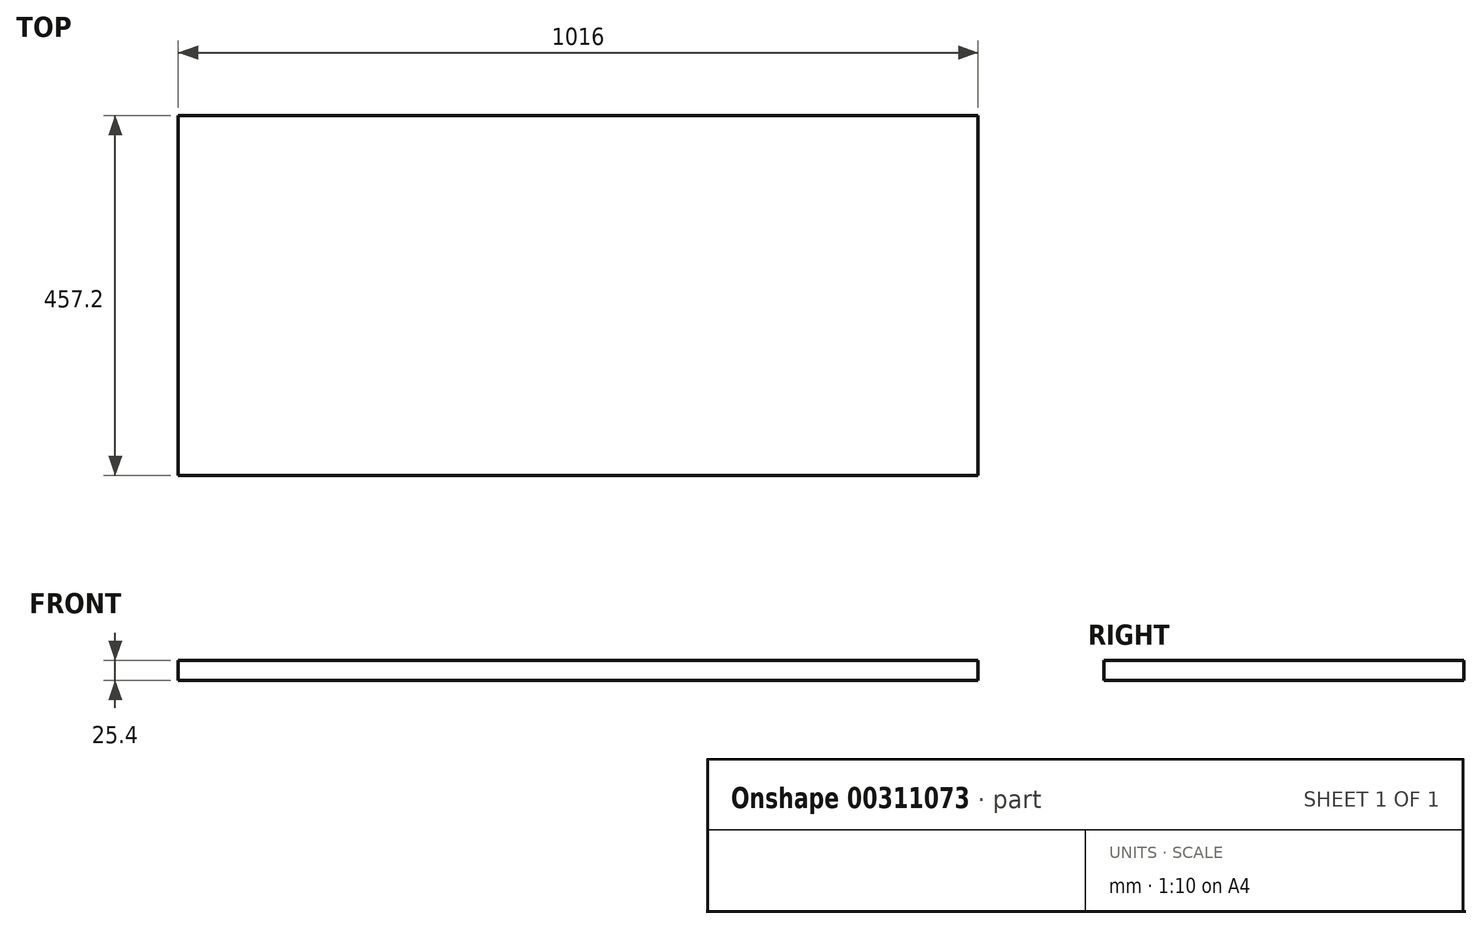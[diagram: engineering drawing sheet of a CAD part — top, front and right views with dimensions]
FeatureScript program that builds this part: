
annotation { "Feature Type Name" : "Feature", "Feature Type Description" : "" }
export const myFeature = defineFeature(function(context is Context, id is Id, definition is map)
    precondition{}
    {
        {
            var Q0;
            Q0=qCreatedBy(makeId("Top.planeOp"),FACE);
            var sketch = newSketch(context, id + "F0", { "sketchPlane" : qUnion([Q0])});
            skLineSegment(sketch, "E0.bottom", {"start": v(0, 0) * mm, "end": v(1016, 0) * mm});
            skLineSegment(sketch, "E0.top", {"start": v(0, 457.2) * mm, "end": v(1016, 457.2) * mm});
            skLineSegment(sketch, "E0.left", {"start": v(0, 0) * mm, "end": v(0, 457.2) * mm});
            skLineSegment(sketch, "E0.right", {"start": v(1016, 0) * mm, "end": v(1016, 457.2) * mm});
            skSolve(sketch);
        }
        {
            var Q0;
            Q0 = qSketchRegion(id + "F0", true);
            extrude(context, id + "F1", {"entities" : qUnion([Q0]), "depth" : 25.4 * mm});
        }
    });
